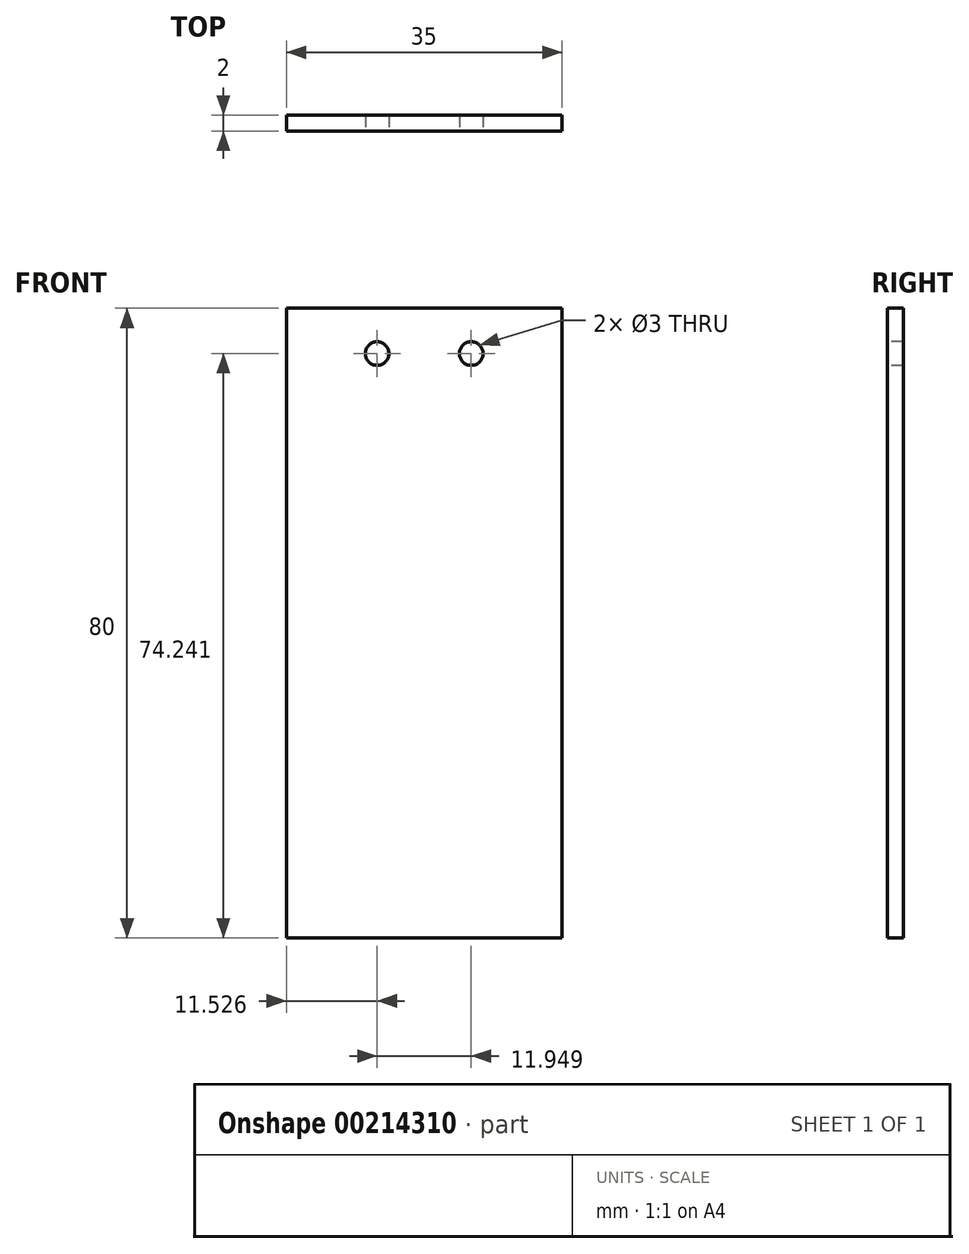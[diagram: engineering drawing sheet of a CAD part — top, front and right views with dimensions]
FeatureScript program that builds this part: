
annotation { "Feature Type Name" : "Feature", "Feature Type Description" : "" }
export const myFeature = defineFeature(function(context is Context, id is Id, definition is map)
    precondition{}
    {
        {
            var Q0;
            Q0=qCreatedBy(makeId("Front.planeOp"),FACE);
            var sketch = newSketch(context, id + "F0", { "sketchPlane" : qUnion([Q0])});
            skLineSegment(sketch, "E0.bottom", {"start": v(17.5, 40) * mm, "end": v(-17.5, 40) * mm});
            skLineSegment(sketch, "E0.top", {"start": v(17.5, -40) * mm, "end": v(-17.5, -40) * mm});
            skLineSegment(sketch, "E0.left", {"start": v(17.5, 40) * mm, "end": v(17.5, -40) * mm});
            skLineSegment(sketch, "E0.right", {"start": v(-17.5, 40) * mm, "end": v(-17.5, -40) * mm});
            skPoint(sketch, "E0.middle", {"position": v(0, 0) * mm});
            skSolve(sketch);
        }
        {
            var Q0;
            Q0 = qSketchRegion(id + "F0", true);
            extrude(context, id + "F1", {"entities" : qUnion([Q0]), "depth" : 2 * mm});
        }
        {
            var Q0;
            Q0=makeQuery(id+"F1.opExtrude","CAP_FACE",FACE,{"disambiguationData":[OSD([sQuery(id+"F0.wireOp",EDGE,"E0.bottom"),sQuery(id+"F0.wireOp",EDGE,"E0.top"),sQuery(id+"F0.wireOp",EDGE,"E0.left"),sQuery(id+"F0.wireOp",EDGE,"E0.right")])],"isStart":false});
            var sketch = newSketch(context, id + "F2", { "sketchPlane" : qUnion([Q0])});
            skLineSegment(sketch, "E1.bottom", {"start": v(5.97, 34.24) * mm, "end": v(-5.97, 34.24) * mm, "construction": true});
            skLineSegment(sketch, "E1.top", {"start": v(5.97, 34.24) * mm, "end": v(-5.97, 34.24) * mm, "construction": true});
            skLineSegment(sketch, "E1.left", {"start": v(5.97, 34.24) * mm, "end": v(5.97, 34.24) * mm});
            skLineSegment(sketch, "E1.right", {"start": v(-5.97, 34.24) * mm, "end": v(-5.97, 34.24) * mm});
            skPoint(sketch, "E1.middle", {"position": v(0, 34.24) * mm});
            skCircle(sketch, "E2", {"center": v(5.97, 34.24) * mm, "radius": 1.5 * mm});
            skCircle(sketch, "E3", {"center": v(-5.97, 34.24) * mm, "radius": 1.5 * mm});
            skSolve(sketch);
        }
        {
            var Q0;
            Q0 = qSketchRegion(id + "F2", true);
            extrude(context, id + "F3", {"entities" : qUnion([Q0]), "operationType" : NewBodyOperationType.REMOVE, "oppositeDirection" : true, "depth" : 25 * mm});
        }
    });
